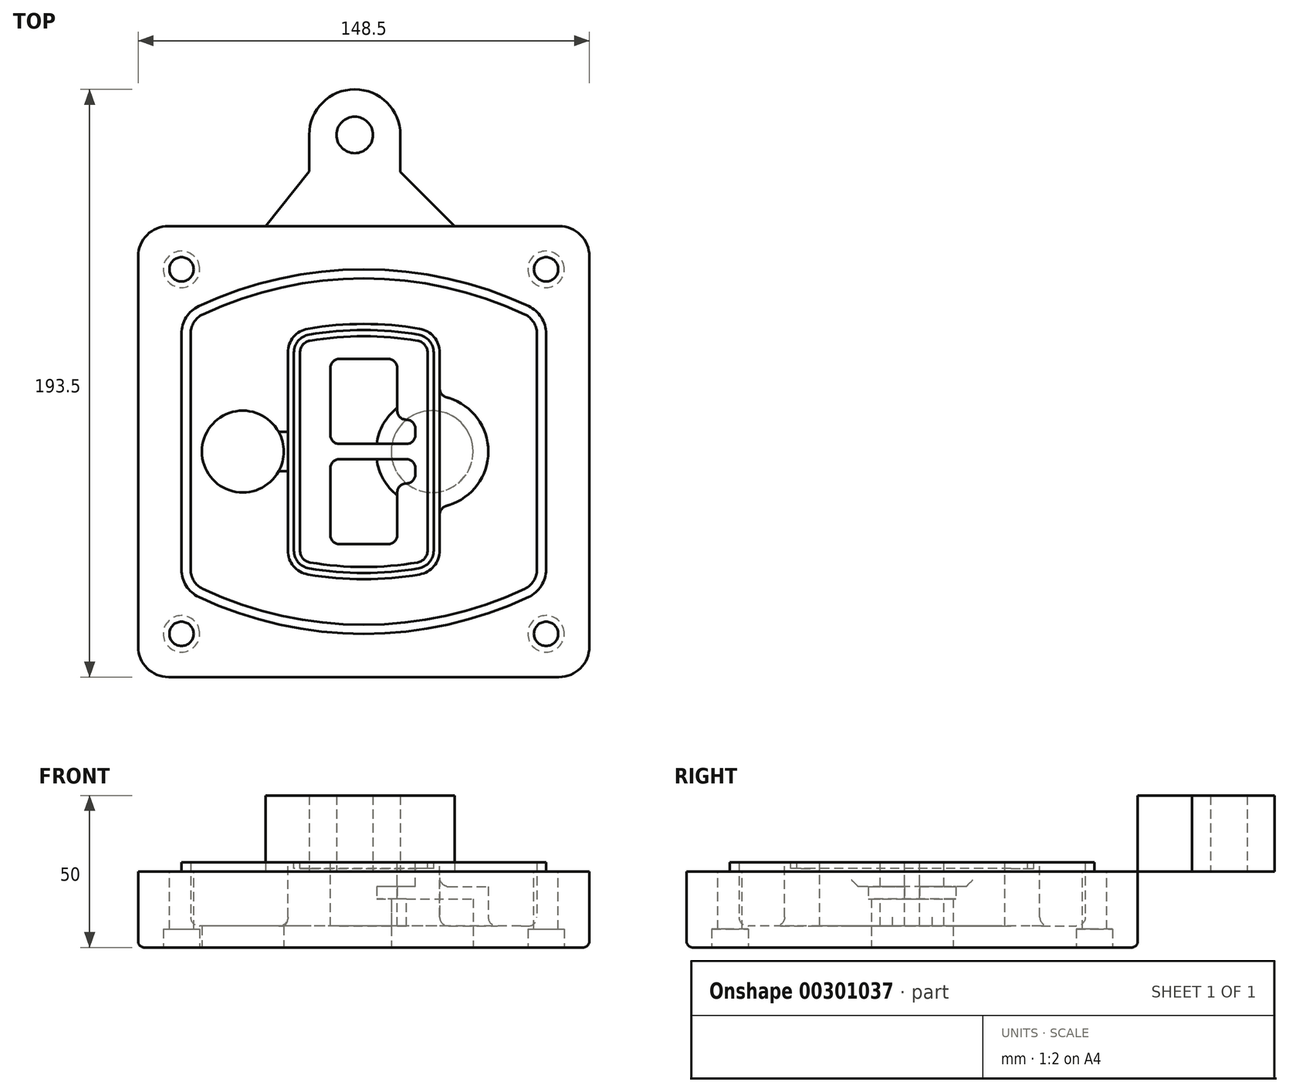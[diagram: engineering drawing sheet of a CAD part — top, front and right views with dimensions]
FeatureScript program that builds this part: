
annotation { "Feature Type Name" : "Feature", "Feature Type Description" : "" }
export const myFeature = defineFeature(function(context is Context, id is Id, definition is map)
    precondition{}
    {
        {
            var Q0;
            Q0=qCreatedBy(makeId("Top.planeOp"),FACE);
            var sketch = newSketch(context, id + "F0", { "sketchPlane" : qUnion([Q0])});
            skPoint(sketch, "E0.rect.middle", {"position": v(0, 0) * mm});
            skLineSegment(sketch, "E1.bottom", {"start": v(-64.25, -74.25) * mm, "end": v(64.25, -74.25) * mm});
            skLineSegment(sketch, "E1.top", {"start": v(-64.25, 74.25) * mm, "end": v(64.25, 74.25) * mm});
            skLineSegment(sketch, "E1.left", {"start": v(-74.25, -64.25) * mm, "end": v(-74.25, 64.25) * mm});
            skLineSegment(sketch, "E1.right", {"start": v(74.25, -64.25) * mm, "end": v(74.25, 64.25) * mm});
            skLineSegment(sketch, "E2", {"start": v(-74.25, 74.25) * mm, "end": v(74.25, -74.25) * mm, "construction": true});
            skLineSegment(sketch, "E3", {"start": v(74.25, 74.25) * mm, "end": v(-74.25, -74.25) * mm, "construction": true});
            skCircle(sketch, "E4", {"center": v(-60, 60) * mm, "radius": 4 * mm});
            skCircle(sketch, "E5", {"center": v(60, 60) * mm, "radius": 4 * mm});
            skCircle(sketch, "E6", {"center": v(60, -60) * mm, "radius": 4 * mm});
            skCircle(sketch, "E7", {"center": v(-60, -60) * mm, "radius": 4 * mm});
            skLineSegment(sketch, "E8", {"start": v(-60, 60) * mm, "end": v(60, 60) * mm, "construction": true});
            skLineSegment(sketch, "E9", {"start": v(60, 60) * mm, "end": v(60, -60) * mm, "construction": true});
            skLineSegment(sketch, "E10", {"start": v(60, -60) * mm, "end": v(-60, -60) * mm, "construction": true});
            skLineSegment(sketch, "E11", {"start": v(-60, -60) * mm, "end": v(-60, 60) * mm, "construction": true});
            skLineSegment(sketch, "E12", {"start": v(-60, 38.83) * mm, "end": v(-60, -38.83) * mm});
            skLineSegment(sketch, "E13", {"start": v(60, 38.83) * mm, "end": v(60, -38.83) * mm});
            skArc(sketch, "E14", {"start": v(54.26, 47.88) * mm, "mid": v(0, 60) * mm, "end": v(-54.26, 47.88) * mm});
            skArc(sketch, "E15", {"start": v(-54.26, -47.88) * mm, "mid": v(0, -60) * mm, "end": v(54.26, -47.88) * mm});
            skLineSegment(sketch, "E16", {"start": v(-60, 0) * mm, "end": v(60, 0) * mm, "construction": true});
            skPoint(sketch, "E17.visualSharp", {"position": v(-60, -45) * mm});
            skArc(sketch, "E17.filletArc", {"start": v(-60, -38.83) * mm, "mid": v(-58.44, -44.2) * mm, "end": v(-54.26, -47.88) * mm});
            skPoint(sketch, "E18.visualSharp", {"position": v(-60, 45) * mm});
            skArc(sketch, "E18.filletArc", {"start": v(-54.26, 47.88) * mm, "mid": v(-58.44, 44.2) * mm, "end": v(-60, 38.83) * mm});
            skPoint(sketch, "E19.visualSharp", {"position": v(60, 45) * mm});
            skArc(sketch, "E19.filletArc", {"start": v(60, 38.83) * mm, "mid": v(58.44, 44.2) * mm, "end": v(54.26, 47.88) * mm});
            skPoint(sketch, "E20.visualSharp", {"position": v(60, -45) * mm});
            skArc(sketch, "E20.filletArc", {"start": v(54.26, -47.88) * mm, "mid": v(58.44, -44.2) * mm, "end": v(60, -38.83) * mm});
            skPoint(sketch, "E21.visualSharp", {"position": v(-74.25, 74.25) * mm});
            skArc(sketch, "E21.filletArc", {"start": v(-64.25, 74.25) * mm, "mid": v(-71.32, 71.32) * mm, "end": v(-74.25, 64.25) * mm});
            skPoint(sketch, "E22.visualSharp", {"position": v(74.25, 74.25) * mm});
            skArc(sketch, "E22.filletArc", {"start": v(74.25, 64.25) * mm, "mid": v(71.32, 71.32) * mm, "end": v(64.25, 74.25) * mm});
            skPoint(sketch, "E23.visualSharp", {"position": v(74.25, -74.25) * mm});
            skArc(sketch, "E23.filletArc", {"start": v(64.25, -74.25) * mm, "mid": v(71.32, -71.32) * mm, "end": v(74.25, -64.25) * mm});
            skPoint(sketch, "E24.visualSharp", {"position": v(-74.25, -74.25) * mm});
            skArc(sketch, "E24.filletArc", {"start": v(-74.25, -64.25) * mm, "mid": v(-71.32, -71.32) * mm, "end": v(-64.25, -74.25) * mm});
            skArc(sketch, "E25.0", {"start": v(57, 38.83) * mm, "mid": v(55.9, 42.58) * mm, "end": v(52.98, 45.17) * mm});
            skLineSegment(sketch, "E25.1", {"start": v(57, 38.83) * mm, "end": v(57, -38.83) * mm});
            skArc(sketch, "E25.2", {"start": v(52.98, -45.17) * mm, "mid": v(55.9, -42.58) * mm, "end": v(57, -38.83) * mm});
            skArc(sketch, "E25.3", {"start": v(-52.98, -45.17) * mm, "mid": v(0, -57) * mm, "end": v(52.98, -45.17) * mm});
            skArc(sketch, "E25.4", {"start": v(-57, -38.83) * mm, "mid": v(-55.9, -42.58) * mm, "end": v(-52.98, -45.17) * mm});
            skArc(sketch, "E25.5", {"start": v(52.98, 45.17) * mm, "mid": v(0, 57) * mm, "end": v(-52.98, 45.17) * mm});
            skLineSegment(sketch, "E25.6", {"start": v(-57, 38.83) * mm, "end": v(-57, -38.83) * mm});
            skArc(sketch, "E25.7", {"start": v(-52.98, 45.17) * mm, "mid": v(-55.9, 42.58) * mm, "end": v(-57, 38.83) * mm});
            skArc(sketch, "E26.0", {"start": v(-55.96, 51.5) * mm, "mid": v(-61.82, 46.33) * mm, "end": v(-64, 38.83) * mm});
            skArc(sketch, "E26.1", {"start": v(55.96, 51.5) * mm, "mid": v(0, 64) * mm, "end": v(-55.96, 51.5) * mm});
            skArc(sketch, "E26.2", {"start": v(64, 38.83) * mm, "mid": v(61.82, 46.33) * mm, "end": v(55.96, 51.5) * mm});
            skLineSegment(sketch, "E26.3", {"start": v(64, 38.83) * mm, "end": v(64, -38.83) * mm});
            skArc(sketch, "E26.4", {"start": v(55.96, -51.5) * mm, "mid": v(61.82, -46.33) * mm, "end": v(64, -38.83) * mm});
            skLineSegment(sketch, "E26.5", {"start": v(-64, 38.83) * mm, "end": v(-64, -38.83) * mm});
            skArc(sketch, "E26.6", {"start": v(-55.96, -51.5) * mm, "mid": v(0, -64) * mm, "end": v(55.96, -51.5) * mm});
            skArc(sketch, "E26.7", {"start": v(-64, -38.83) * mm, "mid": v(-61.82, -46.33) * mm, "end": v(-55.96, -51.5) * mm});
            skSolve(sketch);
        }
        {
            var Q0;
            Q0=makeQuery(id+"F0.imprint","IMPRINT",FACE,{"disambiguationData":[TD([[makeQuery(id+"F0.imprint","IMPRINT",EDGE,{"derivedFrom":sQuery(id+"F0.wireOp",EDGE,"E1.bottom")}),1.0]])]});
            var Q1;
            Q1=makeQuery(id+"F0.imprint","IMPRINT",FACE,{"disambiguationData":[TD([[makeQuery(id+"F0.imprint","IMPRINT",EDGE,{"derivedFrom":sQuery(id+"F0.wireOp",EDGE,"E12")}),1.0]])]});
            var Q2;
            Q2=makeQuery(id+"F0.imprint","IMPRINT",FACE,{"disambiguationData":[TD([[makeQuery(id+"F0.imprint","IMPRINT",EDGE,{"derivedFrom":sQuery(id+"F0.wireOp",EDGE,"E25.0")}),1.0]])]});
            var Q3;
            Q3=makeQuery(id+"F0.imprint","IMPRINT",FACE,{"disambiguationData":[TD([[makeQuery(id+"F0.imprint","IMPRINT",EDGE,{"derivedFrom":sQuery(id+"F0.wireOp",EDGE,"E12")}),-1.0]])]});
            extrude(context, id + "F1", {"entities" : qUnion([Q0, Q1, Q2, Q3]), "oppositeDirection" : true, "depth" : 25 * mm});
        }
        {
            var Q0;
            Q0=makeQuery(id+"F0.imprint","IMPRINT",FACE,{"disambiguationData":[TD([[makeQuery(id+"F0.imprint","IMPRINT",EDGE,{"derivedFrom":sQuery(id+"F0.wireOp",EDGE,"E12")}),1.0]])]});
            extrude(context, id + "F2", {"entities" : qUnion([Q0]), "operationType" : NewBodyOperationType.ADD, "depth" : 3 * mm});
        }
        {
            var Q0;
            Q0=makeQuery(id+"F0.imprint","IMPRINT",FACE,{"disambiguationData":[TD([[makeQuery(id+"F0.imprint","IMPRINT",EDGE,{"derivedFrom":sQuery(id+"F0.wireOp",EDGE,"E25.0")}),1.0]])]});
            extrude(context, id + "F3", {"entities" : qUnion([Q0]), "operationType" : NewBodyOperationType.REMOVE, "oppositeDirection" : true, "depth" : 18 * mm});
        }
        {
            var Q0;
            Q0=makeQuery(id+"F2.opExtrude","CAP_FACE",FACE,{"disambiguationData":[OSD([sQuery(id+"F0.wireOp",EDGE,"E12"),sQuery(id+"F0.wireOp",EDGE,"E13"),sQuery(id+"F0.wireOp",EDGE,"E14"),sQuery(id+"F0.wireOp",EDGE,"E15"),sQuery(id+"F0.wireOp",EDGE,"E17.filletArc"),sQuery(id+"F0.wireOp",EDGE,"E18.filletArc"),sQuery(id+"F0.wireOp",EDGE,"E19.filletArc"),sQuery(id+"F0.wireOp",EDGE,"E20.filletArc"),sQuery(id+"F0.wireOp",EDGE,"E25.0"),sQuery(id+"F0.wireOp",EDGE,"E25.1"),sQuery(id+"F0.wireOp",EDGE,"E25.2"),sQuery(id+"F0.wireOp",EDGE,"E25.3"),sQuery(id+"F0.wireOp",EDGE,"E25.4"),sQuery(id+"F0.wireOp",EDGE,"E25.5"),sQuery(id+"F0.wireOp",EDGE,"E25.6"),sQuery(id+"F0.wireOp",EDGE,"E25.7")])],"isStart":false});
            var sketch = newSketch(context, id + "F4", { "sketchPlane" : qUnion([Q0])});
            skArc(sketch, "E27.0", {"start": v(-18.34, -40.45) * mm, "mid": v(0, -42) * mm, "end": v(18.34, -40.45) * mm});
            skArc(sketch, "E28.0", {"start": v(18.34, 40.45) * mm, "mid": v(0, 42) * mm, "end": v(-18.34, 40.45) * mm});
            skLineSegment(sketch, "E29", {"start": v(-25, 32.57) * mm, "end": v(-25, -32.57) * mm});
            skLineSegment(sketch, "E30", {"start": v(25, 32.57) * mm, "end": v(25, -32.57) * mm});
            skLineSegment(sketch, "E31", {"start": v(-25, 39.1) * mm, "end": v(25, 39.1) * mm, "construction": true});
            skLineSegment(sketch, "E32", {"start": v(-25, -39.1) * mm, "end": v(25, -39.1) * mm, "construction": true});
            skPoint(sketch, "E33.visualSharp", {"position": v(-25, 39.1) * mm});
            skArc(sketch, "E33.filletArc", {"start": v(-18.34, 40.45) * mm, "mid": v(-23.11, 37.73) * mm, "end": v(-25, 32.57) * mm});
            skPoint(sketch, "E34.visualSharp", {"position": v(25, 39.1) * mm});
            skArc(sketch, "E34.filletArc", {"start": v(25, 32.57) * mm, "mid": v(23.11, 37.73) * mm, "end": v(18.34, 40.45) * mm});
            skPoint(sketch, "E35.visualSharp", {"position": v(25, -39.1) * mm});
            skArc(sketch, "E35.filletArc", {"start": v(18.34, -40.45) * mm, "mid": v(23.11, -37.73) * mm, "end": v(25, -32.57) * mm});
            skPoint(sketch, "E36.visualSharp", {"position": v(-25, -39.1) * mm});
            skArc(sketch, "E36.filletArc", {"start": v(-25, -32.57) * mm, "mid": v(-23.11, -37.73) * mm, "end": v(-18.34, -40.45) * mm});
            skArc(sketch, "E37.0", {"start": v(52.98, 45.17) * mm, "mid": v(0, 57) * mm, "end": v(-52.98, 45.17) * mm});
            skArc(sketch, "E37.1", {"start": v(-52.98, 45.17) * mm, "mid": v(-55.9, 42.58) * mm, "end": v(-57, 38.83) * mm});
            skLineSegment(sketch, "E37.2", {"start": v(-57, 38.83) * mm, "end": v(-57, -38.83) * mm});
            skArc(sketch, "E37.3", {"start": v(-57, -38.83) * mm, "mid": v(-55.9, -42.58) * mm, "end": v(-52.98, -45.17) * mm});
            skArc(sketch, "E37.4", {"start": v(-52.98, -45.17) * mm, "mid": v(0, -57) * mm, "end": v(52.98, -45.17) * mm});
            skArc(sketch, "E37.5", {"start": v(52.98, -45.17) * mm, "mid": v(55.9, -42.58) * mm, "end": v(57, -38.83) * mm});
            skLineSegment(sketch, "E37.6", {"start": v(57, 38.83) * mm, "end": v(57, -38.83) * mm});
            skArc(sketch, "E37.7", {"start": v(57, 38.83) * mm, "mid": v(55.9, 42.58) * mm, "end": v(52.98, 45.17) * mm});
            skLineSegment(sketch, "E38.0", {"start": v(23, 32.57) * mm, "end": v(23, -32.57) * mm});
            skArc(sketch, "E38.1", {"start": v(18, -38.48) * mm, "mid": v(21.58, -36.44) * mm, "end": v(23, -32.57) * mm});
            skArc(sketch, "E38.2", {"start": v(-18, -38.48) * mm, "mid": v(0, -40) * mm, "end": v(18, -38.48) * mm});
            skArc(sketch, "E38.3", {"start": v(-23, -32.57) * mm, "mid": v(-21.58, -36.44) * mm, "end": v(-18, -38.48) * mm});
            skLineSegment(sketch, "E38.4", {"start": v(-23, 32.57) * mm, "end": v(-23, -32.57) * mm});
            skArc(sketch, "E38.5", {"start": v(23, 32.57) * mm, "mid": v(21.58, 36.44) * mm, "end": v(18, 38.48) * mm});
            skArc(sketch, "E38.6", {"start": v(-18, 38.48) * mm, "mid": v(-21.58, 36.44) * mm, "end": v(-23, 32.57) * mm});
            skArc(sketch, "E38.7", {"start": v(18, 38.48) * mm, "mid": v(0, 40) * mm, "end": v(-18, 38.48) * mm});
            skArc(sketch, "E39.0", {"start": v(21, 32.57) * mm, "mid": v(20.06, 35.15) * mm, "end": v(17.67, 36.5) * mm});
            skLineSegment(sketch, "E39.1", {"start": v(21, 32.57) * mm, "end": v(21, -32.57) * mm});
            skArc(sketch, "E39.2", {"start": v(17.67, -36.5) * mm, "mid": v(20.06, -35.15) * mm, "end": v(21, -32.57) * mm});
            skArc(sketch, "E39.3", {"start": v(-17.67, -36.5) * mm, "mid": v(0, -38) * mm, "end": v(17.67, -36.5) * mm});
            skArc(sketch, "E39.4", {"start": v(-21, -32.57) * mm, "mid": v(-20.06, -35.15) * mm, "end": v(-17.67, -36.5) * mm});
            skArc(sketch, "E39.5", {"start": v(17.67, 36.5) * mm, "mid": v(0, 38) * mm, "end": v(-17.67, 36.5) * mm});
            skLineSegment(sketch, "E39.6", {"start": v(-21, 32.57) * mm, "end": v(-21, -32.57) * mm});
            skArc(sketch, "E39.7", {"start": v(-17.67, 36.5) * mm, "mid": v(-20.06, 35.15) * mm, "end": v(-21, 32.57) * mm});
            skLineSegment(sketch, "E40", {"start": v(-25, 0) * mm, "end": v(25, 0) * mm, "construction": true});
            skLineSegment(sketch, "E41", {"start": v(-11, 5.5) * mm, "end": v(-11, 27.5) * mm});
            skLineSegment(sketch, "E42", {"start": v(-8, 30.5) * mm, "end": v(8, 30.5) * mm});
            skLineSegment(sketch, "E43", {"start": v(11, 27.5) * mm, "end": v(11, 13.5) * mm});
            skLineSegment(sketch, "E44", {"start": v(14, 10.5) * mm, "end": v(14, 10.5) * mm});
            skLineSegment(sketch, "E45", {"start": v(17, 7.5) * mm, "end": v(17, 5.5) * mm});
            skLineSegment(sketch, "E46", {"start": v(14, 2.5) * mm, "end": v(-8, 2.5) * mm});
            skPoint(sketch, "E47.visualSharp", {"position": v(-11, 30.5) * mm});
            skArc(sketch, "E47.filletArc", {"start": v(-8, 30.5) * mm, "mid": v(-10.12, 29.62) * mm, "end": v(-11, 27.5) * mm});
            skPoint(sketch, "E48.visualSharp", {"position": v(11, 30.5) * mm});
            skArc(sketch, "E48.filletArc", {"start": v(11, 27.5) * mm, "mid": v(10.12, 29.62) * mm, "end": v(8, 30.5) * mm});
            skPoint(sketch, "E49.visualSharp", {"position": v(11, 10.5) * mm});
            skArc(sketch, "E49.filletArc", {"start": v(11, 13.5) * mm, "mid": v(11.88, 11.38) * mm, "end": v(14, 10.5) * mm});
            skPoint(sketch, "E50.visualSharp", {"position": v(17, 10.5) * mm});
            skArc(sketch, "E50.filletArc", {"start": v(17, 7.5) * mm, "mid": v(16.12, 9.62) * mm, "end": v(14, 10.5) * mm});
            skPoint(sketch, "E51.visualSharp", {"position": v(17, 2.5) * mm});
            skArc(sketch, "E51.filletArc", {"start": v(14, 2.5) * mm, "mid": v(16.12, 3.38) * mm, "end": v(17, 5.5) * mm});
            skPoint(sketch, "E52.visualSharp", {"position": v(-11, 2.5) * mm});
            skArc(sketch, "E52.filletArc", {"start": v(-11, 5.5) * mm, "mid": v(-10.12, 3.38) * mm, "end": v(-8, 2.5) * mm});
            skLineSegment(sketch, "E53.0.MirrorCS", {"start": v(14, -2.5) * mm, "end": v(-8, -2.5) * mm});
            skArc(sketch, "E54.0.MirrorCS", {"start": v(-11, -5.5) * mm, "mid": v(-10.12, -3.38) * mm, "end": v(-8, -2.5) * mm});
            skLineSegment(sketch, "E55.0.MirrorCS", {"start": v(-11, -5.5) * mm, "end": v(-11, -27.5) * mm});
            skArc(sketch, "E56.0.MirrorCS", {"start": v(-8, -30.5) * mm, "mid": v(-10.12, -29.62) * mm, "end": v(-11, -27.5) * mm});
            skLineSegment(sketch, "E57.0.MirrorCS", {"start": v(-8, -30.5) * mm, "end": v(8, -30.5) * mm});
            skArc(sketch, "E58.0.MirrorCS", {"start": v(11, -27.5) * mm, "mid": v(10.12, -29.62) * mm, "end": v(8, -30.5) * mm});
            skLineSegment(sketch, "E59.0.MirrorCS", {"start": v(11, -27.5) * mm, "end": v(11, -13.5) * mm});
            skArc(sketch, "E60.0.MirrorCS", {"start": v(11, -13.5) * mm, "mid": v(11.88, -11.38) * mm, "end": v(14, -10.5) * mm});
            skArc(sketch, "E61.0.MirrorCS", {"start": v(17, -7.5) * mm, "mid": v(16.12, -9.62) * mm, "end": v(14, -10.5) * mm});
            skLineSegment(sketch, "E62.0.MirrorCS", {"start": v(17, -7.5) * mm, "end": v(17, -5.5) * mm});
            skArc(sketch, "E63.0.MirrorCS", {"start": v(14, -2.5) * mm, "mid": v(16.12, -3.38) * mm, "end": v(17, -5.5) * mm});
            skSolve(sketch);
        }
        {
            var Q0;
            Q0=makeQuery(id+"F4.imprint","IMPRINT",FACE,{"disambiguationData":[TD([[makeQuery(id+"F4.imprint","IMPRINT",EDGE,{"derivedFrom":sQuery(id+"F4.wireOp",EDGE,"E27.0")}),1.0]])]});
            var Q1;
            Q1=makeQuery(id+"F4.imprint","IMPRINT",FACE,{"disambiguationData":[TD([[makeQuery(id+"F4.imprint","IMPRINT",EDGE,{"derivedFrom":sQuery(id+"F4.wireOp",EDGE,"E38.0")}),-1.0]])]});
            var Q2;
            Q2=makeQuery(id+"F4.imprint","IMPRINT",FACE,{"disambiguationData":[TD([[makeQuery(id+"F4.imprint","IMPRINT",EDGE,{"derivedFrom":sQuery(id+"F4.wireOp",EDGE,"E39.0")}),1.0]])]});
            extrude(context, id + "F5", {"entities" : qUnion([Q0, Q1, Q2]), "operationType" : NewBodyOperationType.ADD, "endBound" : BoundingType.UP_TO_NEXT, "oppositeDirection" : true, "depth" : 25 * mm});
        }
        {
            var Q0;
            Q0=makeQuery(id+"F4.imprint","IMPRINT",FACE,{"disambiguationData":[TD([[makeQuery(id+"F4.imprint","IMPRINT",EDGE,{"derivedFrom":sQuery(id+"F4.wireOp",EDGE,"E38.0")}),-1.0]])]});
            extrude(context, id + "F6", {"entities" : qUnion([Q0]), "operationType" : NewBodyOperationType.REMOVE, "oppositeDirection" : true, "depth" : 2 * mm});
        }
        {
            var Q0;
            Q0=makeQuery(id+"F1.opExtrude","CAP_FACE",FACE,{"disambiguationData":[OSD([sQuery(id+"F0.wireOp",EDGE,"E1.bottom"),sQuery(id+"F0.wireOp",EDGE,"E1.top"),sQuery(id+"F0.wireOp",EDGE,"E1.left"),sQuery(id+"F0.wireOp",EDGE,"E1.right"),sQuery(id+"F0.wireOp",EDGE,"E4"),sQuery(id+"F0.wireOp",EDGE,"E5"),sQuery(id+"F0.wireOp",EDGE,"E6"),sQuery(id+"F0.wireOp",EDGE,"E7"),sQuery(id+"F0.wireOp",EDGE,"E21.filletArc"),sQuery(id+"F0.wireOp",EDGE,"E22.filletArc"),sQuery(id+"F0.wireOp",EDGE,"E23.filletArc"),sQuery(id+"F0.wireOp",EDGE,"E24.filletArc")])],"isStart":false});
            var sketch = newSketch(context, id + "F7", { "sketchPlane" : qUnion([Q0])});
            skCircle(sketch, "E64", {"center": v(22.5, 0) * mm, "radius": 13.47 * mm});
            skCircle(sketch, "E65", {"center": v(-39.81, 0) * mm, "radius": 13.47 * mm});
            skLineSegment(sketch, "E66", {"start": v(74.25, 0) * mm, "end": v(-74.25, 0) * mm});
            skCircle(sketch, "E67", {"center": v(22.5, 0) * mm, "radius": 18.47 * mm});
            skCircle(sketch, "E68", {"center": v(60, -60) * mm, "radius": 6 * mm});
            skCircle(sketch, "E69", {"center": v(-60, -60) * mm, "radius": 6 * mm});
            skCircle(sketch, "E70", {"center": v(-60, 60) * mm, "radius": 6 * mm});
            skCircle(sketch, "E71", {"center": v(60, 60) * mm, "radius": 6 * mm});
            skSolve(sketch);
        }
        {
            var Q0;
            {var subQ1=sQuery(id+"F7.wireOp",EDGE,"E66");var subQ4=sQuery(id+"F7.wireOp",EDGE,"E64");var subQ6=makeQuery(id+"F7.imprint","INTERSECT",VERTEX,{"disambiguationData":[OD(0.0)],"derivedFrom":[subQ4,subQ1]});Q0=makeQuery(id+"F7.imprint","IMPRINT",FACE,{"disambiguationData":[TD([[makeQuery(id+"F7.imprint","IMPRINT",EDGE,{"disambiguationData":[TD([[subQ6,-1.0]])],"derivedFrom":subQ4}),-1.0]])]});}
            var Q1;
            {var subQ0=sQuery(id+"F7.wireOp",EDGE,"E66");var subQ1=sQuery(id+"F7.wireOp",EDGE,"E64");var subQ3=makeQuery(id+"F7.imprint","INTERSECT",VERTEX,{"disambiguationData":[OD(0.0)],"derivedFrom":[subQ1,subQ0]});Q1=makeQuery(id+"F7.imprint","IMPRINT",FACE,{"disambiguationData":[TD([[makeQuery(id+"F7.imprint","IMPRINT",EDGE,{"disambiguationData":[TD([[subQ3,-1.0]])],"derivedFrom":subQ1}),1.0]])]});}
            var Q2;
            {var subQ0=sQuery(id+"F7.wireOp",EDGE,"E66");var subQ1=sQuery(id+"F7.wireOp",EDGE,"E64");var subQ3=makeQuery(id+"F7.imprint","INTERSECT",VERTEX,{"disambiguationData":[OD(0.0)],"derivedFrom":[subQ1,subQ0]});Q2=makeQuery(id+"F7.imprint","IMPRINT",FACE,{"disambiguationData":[TD([[makeQuery(id+"F7.imprint","IMPRINT",EDGE,{"disambiguationData":[TD([[subQ3,1.0]])],"derivedFrom":subQ1}),1.0]])]});}
            var Q3;
            {var subQ1=sQuery(id+"F7.wireOp",EDGE,"E66");var subQ4=sQuery(id+"F7.wireOp",EDGE,"E64");var subQ6=makeQuery(id+"F7.imprint","INTERSECT",VERTEX,{"disambiguationData":[OD(0.0)],"derivedFrom":[subQ4,subQ1]});Q3=makeQuery(id+"F7.imprint","IMPRINT",FACE,{"disambiguationData":[TD([[makeQuery(id+"F7.imprint","IMPRINT",EDGE,{"disambiguationData":[TD([[subQ6,1.0]])],"derivedFrom":subQ4}),-1.0]])]});}
            extrude(context, id + "F8", {"entities" : qUnion([Q0, Q1, Q2, Q3]), "operationType" : NewBodyOperationType.ADD, "oppositeDirection" : true, "depth" : 20 * mm});
        }
        {
            var Q0;
            {var subQ0=sQuery(id+"F7.wireOp",EDGE,"E66");var subQ1=sQuery(id+"F7.wireOp",EDGE,"E64");var subQ3=makeQuery(id+"F7.imprint","INTERSECT",VERTEX,{"disambiguationData":[OD(0.0)],"derivedFrom":[subQ1,subQ0]});Q0=makeQuery(id+"F7.imprint","IMPRINT",FACE,{"disambiguationData":[TD([[makeQuery(id+"F7.imprint","IMPRINT",EDGE,{"disambiguationData":[TD([[subQ3,-1.0]])],"derivedFrom":subQ1}),1.0]])]});}
            var Q1;
            {var subQ0=sQuery(id+"F7.wireOp",EDGE,"E66");var subQ1=sQuery(id+"F7.wireOp",EDGE,"E64");var subQ3=makeQuery(id+"F7.imprint","INTERSECT",VERTEX,{"disambiguationData":[OD(0.0)],"derivedFrom":[subQ1,subQ0]});Q1=makeQuery(id+"F7.imprint","IMPRINT",FACE,{"disambiguationData":[TD([[makeQuery(id+"F7.imprint","IMPRINT",EDGE,{"disambiguationData":[TD([[subQ3,1.0]])],"derivedFrom":subQ1}),1.0]])]});}
            extrude(context, id + "F9", {"entities" : qUnion([Q0, Q1]), "operationType" : NewBodyOperationType.REMOVE, "oppositeDirection" : true, "depth" : 16 * mm});
        }
        {
            var Q0;
            {var subQ0=sQuery(id+"F7.wireOp",EDGE,"E66");var subQ1=sQuery(id+"F7.wireOp",EDGE,"E65");var subQ3=makeQuery(id+"F7.imprint","INTERSECT",VERTEX,{"disambiguationData":[OD(0.0)],"derivedFrom":[subQ1,subQ0]});Q0=makeQuery(id+"F7.imprint","IMPRINT",FACE,{"disambiguationData":[TD([[makeQuery(id+"F7.imprint","IMPRINT",EDGE,{"disambiguationData":[TD([[subQ3,-1.0]])],"derivedFrom":subQ1}),1.0]])]});}
            var Q1;
            {var subQ0=sQuery(id+"F7.wireOp",EDGE,"E66");var subQ1=sQuery(id+"F7.wireOp",EDGE,"E65");var subQ3=makeQuery(id+"F7.imprint","INTERSECT",VERTEX,{"disambiguationData":[OD(0.0)],"derivedFrom":[subQ1,subQ0]});Q1=makeQuery(id+"F7.imprint","IMPRINT",FACE,{"disambiguationData":[TD([[makeQuery(id+"F7.imprint","IMPRINT",EDGE,{"disambiguationData":[TD([[subQ3,1.0]])],"derivedFrom":subQ1}),1.0]])]});}
            extrude(context, id + "F10", {"entities" : qUnion([Q0, Q1]), "operationType" : NewBodyOperationType.REMOVE, "oppositeDirection" : true, "depth" : 25 * mm});
        }
        {
            var Q0;
            Q0=makeQuery(id+"F7.imprint","IMPRINT",FACE,{"disambiguationData":[TD([[makeQuery(id+"F7.imprint","IMPRINT",EDGE,{"derivedFrom":sQuery(id+"F7.wireOp",EDGE,"E68")}),1.0]])]});
            var Q1;
            Q1=makeQuery(id+"F7.imprint","IMPRINT",FACE,{"disambiguationData":[TD([[makeQuery(id+"F7.imprint","IMPRINT",EDGE,{"derivedFrom":makeQuery(id+"F1.opExtrude","CAP_EDGE",EDGE,{"disambiguationData":[OSD([sQuery(id+"F0.wireOp",EDGE,"E5")])],"isStart":false})}),-1.0]])]});
            var Q2;
            Q2=makeQuery(id+"F7.imprint","IMPRINT",FACE,{"disambiguationData":[TD([[makeQuery(id+"F7.imprint","IMPRINT",EDGE,{"derivedFrom":sQuery(id+"F7.wireOp",EDGE,"E69")}),1.0]])]});
            var Q3;
            Q3=makeQuery(id+"F7.imprint","IMPRINT",FACE,{"disambiguationData":[TD([[makeQuery(id+"F7.imprint","IMPRINT",EDGE,{"derivedFrom":makeQuery(id+"F1.opExtrude","CAP_EDGE",EDGE,{"disambiguationData":[OSD([sQuery(id+"F0.wireOp",EDGE,"E4")])],"isStart":false})}),-1.0]])]});
            var Q4;
            Q4=makeQuery(id+"F7.imprint","IMPRINT",FACE,{"disambiguationData":[TD([[makeQuery(id+"F7.imprint","IMPRINT",EDGE,{"derivedFrom":sQuery(id+"F7.wireOp",EDGE,"E70")}),1.0]])]});
            var Q5;
            Q5=makeQuery(id+"F7.imprint","IMPRINT",FACE,{"disambiguationData":[TD([[makeQuery(id+"F7.imprint","IMPRINT",EDGE,{"derivedFrom":makeQuery(id+"F1.opExtrude","CAP_EDGE",EDGE,{"disambiguationData":[OSD([sQuery(id+"F0.wireOp",EDGE,"E7")])],"isStart":false})}),-1.0]])]});
            var Q6;
            Q6=makeQuery(id+"F7.imprint","IMPRINT",FACE,{"disambiguationData":[TD([[makeQuery(id+"F7.imprint","IMPRINT",EDGE,{"derivedFrom":sQuery(id+"F7.wireOp",EDGE,"E71")}),1.0]])]});
            var Q7;
            Q7=makeQuery(id+"F7.imprint","IMPRINT",FACE,{"disambiguationData":[TD([[makeQuery(id+"F7.imprint","IMPRINT",EDGE,{"derivedFrom":makeQuery(id+"F1.opExtrude","CAP_EDGE",EDGE,{"disambiguationData":[OSD([sQuery(id+"F0.wireOp",EDGE,"E6")])],"isStart":false})}),-1.0]])]});
            extrude(context, id + "F11", {"entities" : qUnion([Q0, Q1, Q2, Q3, Q4, Q5, Q6, Q7]), "operationType" : NewBodyOperationType.REMOVE, "oppositeDirection" : true, "depth" : 6 * mm});
        }
        {
            var Q0;
            Q0=makeQuery(id+"F9.boolean.opBoolean","COPY",FACE,{"derivedFrom":makeQuery(id+"F9.opExtrude","CAP_FACE",FACE,{"disambiguationData":[OSD([sQuery(id+"F7.wireOp",EDGE,"E64")])],"isStart":false})});
            var sketch = newSketch(context, id + "F12", { "sketchPlane" : qUnion([Q0])});
            skArc(sketch, "E72.0", {"start": v(11, 14.45) * mm, "mid": v(6.45, 9.13) * mm, "end": v(4.2, 2.5) * mm});
            skArc(sketch, "E72.1", {"start": v(4.2, -2.5) * mm, "mid": v(6.45, -9.13) * mm, "end": v(11, -14.45) * mm});
            skLineSegment(sketch, "E73", {"start": v(4.2, -2.5) * mm, "end": v(14, -2.5) * mm});
            skLineSegment(sketch, "E74.0", {"start": v(14, 2.5) * mm, "end": v(4.2, 2.5) * mm});
            skArc(sketch, "E74.1", {"start": v(14, 2.5) * mm, "mid": v(16.12, 3.38) * mm, "end": v(17, 5.5) * mm});
            skLineSegment(sketch, "E74.2", {"start": v(17, 7.5) * mm, "end": v(17, 5.5) * mm});
            skArc(sketch, "E74.3", {"start": v(17, 7.5) * mm, "mid": v(16.12, 9.62) * mm, "end": v(14, 10.5) * mm});
            skArc(sketch, "E74.4", {"start": v(11, 13.5) * mm, "mid": v(11.88, 11.38) * mm, "end": v(14, 10.5) * mm});
            skLineSegment(sketch, "E74.5", {"start": v(11, 14.45) * mm, "end": v(11, 13.5) * mm});
            skLineSegment(sketch, "E74.7", {"start": v(14, -2.5) * mm, "end": v(4.2, -2.5) * mm});
            skArc(sketch, "E74.8", {"start": v(14, -2.5) * mm, "mid": v(16.12, -3.38) * mm, "end": v(17, -5.5) * mm});
            skLineSegment(sketch, "E74.9", {"start": v(17, -7.5) * mm, "end": v(17, -5.5) * mm});
            skArc(sketch, "E74.10", {"start": v(17, -7.5) * mm, "mid": v(16.12, -9.62) * mm, "end": v(14, -10.5) * mm});
            skArc(sketch, "E74.11", {"start": v(11, -13.5) * mm, "mid": v(11.88, -11.38) * mm, "end": v(14, -10.5) * mm});
            skLineSegment(sketch, "E74.12", {"start": v(11, -14.45) * mm, "end": v(11, -13.5) * mm});
            skPoint(sketch, "E75.orphan", {"position": v(11, -27.5) * mm});
            skPoint(sketch, "E76.orphan", {"position": v(-8, -2.5) * mm});
            skPoint(sketch, "E77.orphan", {"position": v(-8, 2.5) * mm});
            skPoint(sketch, "E78.orphan", {"position": v(11, 27.5) * mm});
            skSolve(sketch);
        }
        {
            var Q0;
            {var subQ7=sQuery(id+"F12.wireOp",EDGE,"E72.0");var subQ14=sQuery(id+"F12.wireOp",EDGE,"E72.1");var subQ16=sQuery(id+"F12.wireOp",EDGE,"E74.1");var subQ18=sQuery(id+"F12.wireOp",EDGE,"E74.8");Q0=qUnion([makeQuery(id+"F12.imprint","IMPRINT",FACE,{"disambiguationData":[TD([[makeQuery(id+"F12.imprint","IMPRINT",EDGE,{"derivedFrom":subQ7}),1.0]])]}),makeQuery(id+"F12.imprint","IMPRINT",FACE,{"disambiguationData":[TD([[makeQuery(id+"F12.imprint","IMPRINT",EDGE,{"derivedFrom":subQ14}),1.0]])]}),makeQuery(id+"F12.imprint","IMPRINT",FACE,{"disambiguationData":[TD([[makeQuery(id+"F12.imprint","IMPRINT",EDGE,{"derivedFrom":subQ16}),1.0]])]}),makeQuery(id+"F12.imprint","IMPRINT",FACE,{"disambiguationData":[TD([[makeQuery(id+"F12.imprint","IMPRINT",EDGE,{"derivedFrom":subQ18}),-1.0]])]})]);}
            var Q1;
            Q1=makeQuery(id+"F5.boolean.opBoolean","SPLIT",FACE,{"disambiguationData":[TD([makeQuery(id+"F5.opExtrude","SWEPT_FACE",FACE,{"disambiguationData":[OSD([sQuery(id+"F4.wireOp",EDGE,"E41")])]})])],"derivedFrom":makeQuery(id+"F3.boolean.opBoolean","COPY",FACE,{"derivedFrom":makeQuery(id+"F3.opExtrude","CAP_FACE",FACE,{"disambiguationData":[OSD([sQuery(id+"F0.wireOp",EDGE,"E25.0"),sQuery(id+"F0.wireOp",EDGE,"E25.1"),sQuery(id+"F0.wireOp",EDGE,"E25.2"),sQuery(id+"F0.wireOp",EDGE,"E25.3"),sQuery(id+"F0.wireOp",EDGE,"E25.4"),sQuery(id+"F0.wireOp",EDGE,"E25.5"),sQuery(id+"F0.wireOp",EDGE,"E25.6"),sQuery(id+"F0.wireOp",EDGE,"E25.7")])],"isStart":false})})});
            extrude(context, id + "F13", {"entities" : qUnion([Q0]), "operationType" : NewBodyOperationType.REMOVE, "endBound" : BoundingType.UP_TO_SURFACE, "endBoundEntityFace" : qUnion([Q1]), "depth" : 25 * mm});
        }
        {
            var Q0;
            Q0=makeQuery(id+"F3.boolean.opBoolean","COPY",EDGE,{"derivedFrom":makeQuery(id+"F3.opExtrude","CAP_EDGE",EDGE,{"disambiguationData":[OSD([sQuery(id+"F0.wireOp",EDGE,"E25.6")])],"isStart":false})});
            var Q1;
            Q1=makeQuery(id+"F8.boolean.opBoolean","INTERSECT",EDGE,{"derivedFrom":[makeQuery(id+"F5.opExtrude","SWEPT_FACE",FACE,{"disambiguationData":[OSD([sQuery(id+"F4.wireOp",EDGE,"E30")])]}),makeQuery(id+"F8.opExtrude","CAP_FACE",FACE,{"disambiguationData":[OSD([sQuery(id+"F7.wireOp",EDGE,"E67")])],"isStart":false})]});
            var Q2;
            Q2=makeQuery(id+"F8.boolean.opBoolean","INTERSECT",EDGE,{"disambiguationData":[OD(1.0)],"derivedFrom":[makeQuery(id+"F5.opExtrude","SWEPT_FACE",FACE,{"disambiguationData":[OSD([sQuery(id+"F4.wireOp",EDGE,"E30")])]}),makeQuery(id+"F8.opExtrude","SWEPT_FACE",FACE,{"disambiguationData":[OSD([sQuery(id+"F7.wireOp",EDGE,"E67")])]})]});
            var Q3;
            {var subQ0=sQuery(id+"F4.wireOp",EDGE,"E30");Q3=makeQuery(id+"F8.boolean.opBoolean","SPLIT",EDGE,{"disambiguationData":[TD([makeQuery(id+"F5.opExtrude","SWEPT_FACE",FACE,{"disambiguationData":[OSD([sQuery(id+"F4.wireOp",EDGE,"E35.filletArc")])]})])],"derivedFrom":makeQuery(id+"F5.opExtrude","CAP_EDGE",EDGE,{"disambiguationData":[OSD([subQ0])],"isStart":false})});}
            var Q4;
            {var subQ0=sQuery(id+"F0.wireOp",EDGE,"E25.7");var subQ1=sQuery(id+"F0.wireOp",EDGE,"E25.1");var subQ2=sQuery(id+"F0.wireOp",EDGE,"E25.6");var subQ3=sQuery(id+"F0.wireOp",EDGE,"E25.5");var subQ4=sQuery(id+"F0.wireOp",EDGE,"E25.4");var subQ5=sQuery(id+"F0.wireOp",EDGE,"E25.0");var subQ6=sQuery(id+"F0.wireOp",EDGE,"E25.2");var subQ7=sQuery(id+"F0.wireOp",EDGE,"E25.3");Q4=makeQuery(id+"F8.boolean.opBoolean","INTERSECT",EDGE,{"derivedFrom":[makeQuery(id+"F5.boolean.opBoolean","SPLIT",FACE,{"disambiguationData":[TD([makeQuery(id+"F2.opExtrude","SWEPT_FACE",FACE,{"disambiguationData":[OSD([subQ5])]})])],"derivedFrom":makeQuery(id+"F3.boolean.opBoolean","COPY",FACE,{"derivedFrom":makeQuery(id+"F3.opExtrude","CAP_FACE",FACE,{"disambiguationData":[OSD([subQ5,subQ1,subQ6,subQ7,subQ4,subQ3,subQ2,subQ0])],"isStart":false})})}),makeQuery(id+"F8.opExtrude","SWEPT_FACE",FACE,{"disambiguationData":[OSD([sQuery(id+"F7.wireOp",EDGE,"E67")])]})]});}
            var Q5;
            Q5=makeQuery(id+"F8.boolean.opBoolean","INTERSECT",EDGE,{"disambiguationData":[OD(0.0)],"derivedFrom":[makeQuery(id+"F5.opExtrude","SWEPT_FACE",FACE,{"disambiguationData":[OSD([sQuery(id+"F4.wireOp",EDGE,"E30")])]}),makeQuery(id+"F8.opExtrude","SWEPT_FACE",FACE,{"disambiguationData":[OSD([sQuery(id+"F7.wireOp",EDGE,"E67")])]})]});
            fillet(context, id + "F14", {"entities" : qUnion([Q0, Q1, Q2, Q3, Q4, Q5]), "radius" : 3 * mm, "tangentPropagation" : true, "allowEdgeOverflow" : false});
        }
        {
            var Q0;
            Q0=makeQuery(id+"F1.opExtrude","CAP_EDGE",EDGE,{"disambiguationData":[OSD([sQuery(id+"F0.wireOp",EDGE,"E1.bottom")])],"isStart":false});
            fillet(context, id + "F15", {"entities" : qUnion([Q0]), "radius" : 2 * mm, "tangentPropagation" : true, "allowEdgeOverflow" : false});
        }
        {
            var Q0;
            {var subQ0=sQuery(id+"F0.wireOp",EDGE,"E21.filletArc");var subQ1=sQuery(id+"F0.wireOp",EDGE,"E7");var subQ2=sQuery(id+"F0.wireOp",EDGE,"E6");var subQ3=sQuery(id+"F0.wireOp",EDGE,"E5");var subQ4=sQuery(id+"F0.wireOp",EDGE,"E4");var subQ5=sQuery(id+"F0.wireOp",EDGE,"E22.filletArc");var subQ6=sQuery(id+"F0.wireOp",EDGE,"E1.bottom");var subQ7=sQuery(id+"F0.wireOp",EDGE,"E1.right");var subQ8=sQuery(id+"F0.wireOp",EDGE,"E1.top");var subQ9=sQuery(id+"F0.wireOp",EDGE,"E1.left");var subQ10=sQuery(id+"F0.wireOp",EDGE,"E23.filletArc");var subQ11=sQuery(id+"F0.wireOp",EDGE,"E24.filletArc");Q0=makeQuery(id+"F2.boolean.opBoolean","SPLIT",FACE,{"disambiguationData":[TD([makeQuery(id+"F1.opExtrude","SWEPT_FACE",FACE,{"disambiguationData":[OSD([subQ6])]})])],"derivedFrom":makeQuery(id+"F1.opExtrude","CAP_FACE",FACE,{"disambiguationData":[OSD([subQ6,subQ8,subQ9,subQ7,subQ4,subQ3,subQ2,subQ1,subQ0,subQ5,subQ10,subQ11])],"isStart":true})});}
            var sketch = newSketch(context, id + "F16", { "sketchPlane" : qUnion([Q0])});
            skLineSegment(sketch, "E79", {"start": v(-32.32, 74.25) * mm, "end": v(-17.97, 92.25) * mm});
            skLineSegment(sketch, "E80", {"start": v(-17.97, 92.25) * mm, "end": v(-17.97, 104.25) * mm});
            skLineSegment(sketch, "E81", {"start": v(12.03, 92.13) * mm, "end": v(12.03, 104.25) * mm});
            skArc(sketch, "E82", {"start": v(12.03, 104.25) * mm, "mid": v(-2.97, 119.25) * mm, "end": v(-17.97, 104.25) * mm});
            skCircle(sketch, "E83", {"center": v(-2.97, 104.25) * mm, "radius": 6 * mm});
            skLineSegment(sketch, "E84", {"start": v(12.03, 92.13) * mm, "end": v(29.9, 74.25) * mm});
            skLineSegment(sketch, "E85", {"start": v(-2.97, 104.25) * mm, "end": v(-2.97, 74.25) * mm, "construction": true});
            skLineSegment(sketch, "E86", {"start": v(-74.25, 0) * mm, "end": v(74.25, 0) * mm, "construction": true});
            skArc(sketch, "E87.MirrorCS", {"start": v(12.03, -104.25) * mm, "mid": v(-2.97, -119.25) * mm, "end": v(-17.97, -104.25) * mm});
            skLineSegment(sketch, "E88.MirrorCS", {"start": v(-17.97, -92.25) * mm, "end": v(-17.97, -104.25) * mm});
            skLineSegment(sketch, "E89.MirrorCS", {"start": v(12.03, -92.13) * mm, "end": v(12.03, -104.25) * mm});
            skLineSegment(sketch, "E90.MirrorCS", {"start": v(-32.32, -74.25) * mm, "end": v(-17.97, -92.25) * mm});
            skLineSegment(sketch, "E91.MirrorCS", {"start": v(12.03, -92.13) * mm, "end": v(29.9, -74.25) * mm});
            skLineSegment(sketch, "E92.MirrorCS", {"start": v(-2.97, -104.25) * mm, "end": v(-2.97, -74.25) * mm, "construction": true});
            skCircle(sketch, "E93.MirrorC", {"center": v(-2.97, -104.25) * mm, "radius": 6 * mm});
            skSolve(sketch);
        }
        {
            var Q0;
            {var subQ0=sQuery(id+"F16.wireOp",EDGE,"E79");Q0=makeQuery(id+"F16.imprint","IMPRINT",FACE,{"disambiguationData":[TD([[makeQuery(id+"F16.imprint","IMPRINT",EDGE,{"derivedFrom":subQ0}),-1.0]])]});}
            var Q1;
            Q1=makeQuery(id+"F16.imprint","IMPRINT",FACE,{"disambiguationData":[TD([[makeQuery(id+"F16.imprint","IMPRINT",EDGE,{"derivedFrom":sQuery(id+"F16.wireOp",EDGE,"E87.MirrorCS")}),-1.0]])]});
            extrude(context, id + "F17", {"entities" : qUnion([Q0, Q1]), "depth" : 25 * mm});
        }
    });
